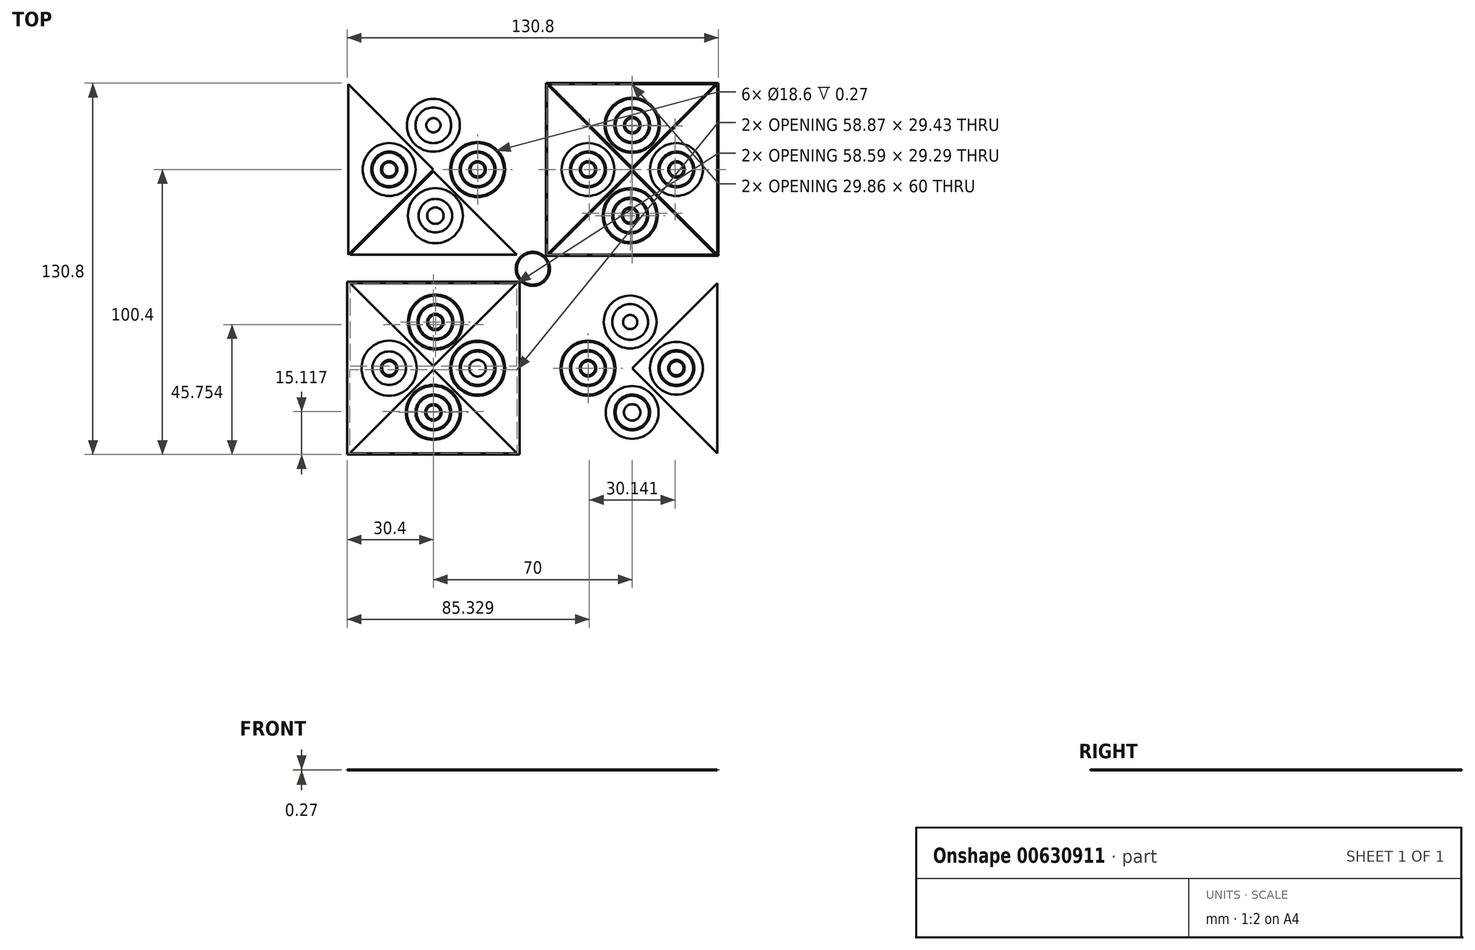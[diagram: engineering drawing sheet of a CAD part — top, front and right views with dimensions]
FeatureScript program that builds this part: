
annotation { "Feature Type Name" : "Feature", "Feature Type Description" : "" }
export const myFeature = defineFeature(function(context is Context, id is Id, definition is map)
    precondition{}
    {
        {
            var Q0;
            Q0=qCreatedBy(makeId("Top.planeOp"),FACE);
            var sketch = newSketch(context, id + "F0", { "sketchPlane" : qUnion([Q0])});
            skLineSegment(sketch, "E0.bottom", {"start": v(70, -70) * mm, "end": v(-70, -70) * mm});
            skLineSegment(sketch, "E0.top", {"start": v(70, 70) * mm, "end": v(-70, 70) * mm});
            skLineSegment(sketch, "E0.left", {"start": v(70, -70) * mm, "end": v(70, 70) * mm});
            skLineSegment(sketch, "E0.right", {"start": v(-70, -70) * mm, "end": v(-70, 70) * mm});
            skPoint(sketch, "E0.middle", {"position": v(0, 0) * mm});
            skLineSegment(sketch, "E1.bottom", {"start": v(-5.57, -65) * mm, "end": v(-64.43, -65) * mm});
            skLineSegment(sketch, "E1.top", {"start": v(-5.7, -5) * mm, "end": v(-64.3, -5) * mm});
            skLineSegment(sketch, "E1.left", {"start": v(-5, -65) * mm, "end": v(-5, -5) * mm});
            skLineSegment(sketch, "E1.right", {"start": v(-65, -65) * mm, "end": v(-65, -5) * mm});
            skPoint(sketch, "E1.middle", {"position": v(-35, -35) * mm});
            skLineSegment(sketch, "E2", {"start": v(-65, -5) * mm, "end": v(-35.14, -34.86) * mm});
            skLineSegment(sketch, "E3", {"start": v(-34.86, -35.14) * mm, "end": v(-5, -65) * mm});
            skLineSegment(sketch, "E4", {"start": v(-65, -65) * mm, "end": v(-35.14, -35.14) * mm});
            skLineSegment(sketch, "E5", {"start": v(-5, -5) * mm, "end": v(-34.86, -34.86) * mm});
            skLineSegment(sketch, "E6.0", {"start": v(-4.6, 0) * mm, "end": v(-70, 0) * mm});
            skLineSegment(sketch, "E6.1", {"start": v(0, -70) * mm, "end": v(0, -4.6) * mm});
            skLineSegment(sketch, "E6.2", {"start": v(0, -70) * mm, "end": v(-70, -70) * mm});
            skLineSegment(sketch, "E6.3", {"start": v(-70, -70) * mm, "end": v(-70, 0) * mm});
            skLineSegment(sketch, "E7.0", {"start": v(-4.6, -4.6) * mm, "end": v(-65.4, -4.6) * mm});
            skLineSegment(sketch, "E7.1", {"start": v(-4.6, -65.4) * mm, "end": v(-4.6, -4.6) * mm});
            skLineSegment(sketch, "E7.2", {"start": v(-4.6, -65.4) * mm, "end": v(-65.4, -65.4) * mm});
            skLineSegment(sketch, "E7.3", {"start": v(-65.4, -65.4) * mm, "end": v(-65.4, -4.6) * mm});
            skLineSegment(sketch, "E8.0", {"start": v(-35, -35.57) * mm, "end": v(-5.57, -65) * mm});
            skLineSegment(sketch, "E8.1", {"start": v(-64.43, -65) * mm, "end": v(-35, -35.57) * mm});
            skLineSegment(sketch, "E9.0", {"start": v(-64.3, -5) * mm, "end": v(-35, -34.3) * mm});
            skLineSegment(sketch, "E9.1", {"start": v(-5.7, -5) * mm, "end": v(-35, -34.3) * mm});
            skArc(sketch, "E10", {"start": v(-35.14, -34.86) * mm, "mid": v(-35.2, -35) * mm, "end": v(-35.14, -35.14) * mm});
            skArc(sketch, "E11.trimOffspring", {"start": v(-34.86, -35.14) * mm, "mid": v(-34.8, -35) * mm, "end": v(-34.86, -34.86) * mm});
            skPoint(sketch, "E12.MirrorCS.end.orphan", {"position": v(-11.42, -33.04) * mm});
            skPoint(sketch, "E12.MirrorCS.start.orphan", {"position": v(-26.98, -37.19) * mm});
            skPoint(sketch, "E13.end.orphan", {"position": v(-36.96, -58.58) * mm});
            skPoint(sketch, "E13.start.orphan", {"position": v(-32.81, -43.02) * mm});
            skCircle(sketch, "E14", {"center": v(-35, -50.57) * mm, "radius": 2.5 * mm});
            skCircle(sketch, "E15.0", {"center": v(-35, -50.57) * mm, "radius": 2.9 * mm});
            skCircle(sketch, "E16.0", {"center": v(-35, -50.57) * mm, "radius": 5.9 * mm});
            skCircle(sketch, "E17.0", {"center": v(-35, -50.57) * mm, "radius": 6.3 * mm});
            skCircle(sketch, "E18.0", {"center": v(-35, -50.57) * mm, "radius": 9.3 * mm});
            skCircle(sketch, "E19.0", {"center": v(-35, -50.57) * mm, "radius": 9.7 * mm});
            skCircle(sketch, "E20.MirrorC", {"center": v(-19.43, -35) * mm, "radius": 9.7 * mm});
            skCircle(sketch, "E21.MirrorC", {"center": v(-19.43, -35) * mm, "radius": 9.3 * mm});
            skCircle(sketch, "E22.MirrorC", {"center": v(-19.43, -35) * mm, "radius": 6.3 * mm});
            skCircle(sketch, "E23.MirrorC", {"center": v(-19.43, -35) * mm, "radius": 5.9 * mm});
            skCircle(sketch, "E24.MirrorC", {"center": v(-19.43, -35) * mm, "radius": 2.9 * mm});
            skCircle(sketch, "E25.MirrorC", {"center": v(-19.43, -35) * mm, "radius": 2.5 * mm});
            skCircle(sketch, "E26.MirrorC", {"center": v(-50.57, -35) * mm, "radius": 9.7 * mm});
            skCircle(sketch, "E27.MirrorC", {"center": v(-50.57, -35) * mm, "radius": 9.3 * mm});
            skCircle(sketch, "E28.MirrorC", {"center": v(-50.57, -35) * mm, "radius": 5.9 * mm});
            skCircle(sketch, "E29.MirrorC", {"center": v(-50.57, -35) * mm, "radius": 6.3 * mm});
            skCircle(sketch, "E30.MirrorC", {"center": v(-50.57, -35) * mm, "radius": 2.5 * mm});
            skCircle(sketch, "E31.MirrorC", {"center": v(-50.57, -35) * mm, "radius": 2.9 * mm});
            skCircle(sketch, "E32.MirrorC", {"center": v(-34.3, -18.73) * mm, "radius": 9.7 * mm});
            skCircle(sketch, "E33.MirrorC", {"center": v(-34.3, -18.73) * mm, "radius": 9.3 * mm});
            skCircle(sketch, "E34.MirrorC", {"center": v(-34.3, -18.73) * mm, "radius": 5.9 * mm});
            skCircle(sketch, "E35.MirrorC", {"center": v(-34.3, -18.73) * mm, "radius": 6.3 * mm});
            skCircle(sketch, "E36.MirrorC", {"center": v(-34.3, -18.73) * mm, "radius": 2.5 * mm});
            skCircle(sketch, "E37.MirrorC", {"center": v(-34.3, -18.73) * mm, "radius": 2.9 * mm});
            skArc(sketch, "E38.MirrorCS", {"start": v(-35.14, 34.86) * mm, "mid": v(-35.2, 35) * mm, "end": v(-35.14, 35.14) * mm});
            skArc(sketch, "E39.MirrorCS", {"start": v(-34.86, 35.14) * mm, "mid": v(-34.8, 35) * mm, "end": v(-34.86, 34.86) * mm});
            skCircle(sketch, "E40.MirrorC", {"center": v(-34.3, 18.73) * mm, "radius": 2.9 * mm});
            skCircle(sketch, "E41.MirrorC", {"center": v(-34.3, 18.73) * mm, "radius": 2.5 * mm});
            skCircle(sketch, "E42.MirrorC", {"center": v(-35, 50.57) * mm, "radius": 2.5 * mm});
            skCircle(sketch, "E43.MirrorC", {"center": v(-35, 50.57) * mm, "radius": 2.9 * mm});
            skCircle(sketch, "E44.MirrorC", {"center": v(-19.43, 35) * mm, "radius": 2.9 * mm});
            skCircle(sketch, "E45.MirrorC", {"center": v(-50.57, 35) * mm, "radius": 2.5 * mm});
            skCircle(sketch, "E46.MirrorC", {"center": v(-50.57, 35) * mm, "radius": 2.9 * mm});
            skCircle(sketch, "E47.MirrorC", {"center": v(-19.43, 35) * mm, "radius": 2.5 * mm});
            skCircle(sketch, "E48.MirrorC", {"center": v(-34.3, 18.73) * mm, "radius": 9.3 * mm});
            skLineSegment(sketch, "E49.MirrorCS", {"start": v(-5.57, 65) * mm, "end": v(-64.43, 65) * mm});
            skLineSegment(sketch, "E50.MirrorCS", {"start": v(-5.7, 5) * mm, "end": v(-64.3, 5) * mm});
            skLineSegment(sketch, "E51.MirrorCS", {"start": v(-5, 65) * mm, "end": v(-5, 5) * mm});
            skLineSegment(sketch, "E52.MirrorCS", {"start": v(-34.86, 35.14) * mm, "end": v(-5, 65) * mm});
            skLineSegment(sketch, "E53.MirrorCS", {"start": v(-65, 65) * mm, "end": v(-35.14, 35.14) * mm});
            skLineSegment(sketch, "E54.MirrorCS", {"start": v(-65.4, 65.4) * mm, "end": v(-65.4, 4.6) * mm});
            skCircle(sketch, "E55.MirrorC", {"center": v(-35, 50.57) * mm, "radius": 9.3 * mm});
            skPoint(sketch, "E56.MirrorP", {"position": v(-32.81, 43.02) * mm});
            skCircle(sketch, "E57.MirrorC", {"center": v(-50.57, 35) * mm, "radius": 5.9 * mm});
            skCircle(sketch, "E58.MirrorC", {"center": v(-35, 50.57) * mm, "radius": 6.3 * mm});
            skCircle(sketch, "E59.MirrorC", {"center": v(-19.43, 35) * mm, "radius": 5.9 * mm});
            skCircle(sketch, "E60.MirrorC", {"center": v(-34.3, 18.73) * mm, "radius": 9.7 * mm});
            skCircle(sketch, "E61.MirrorC", {"center": v(-35, 50.57) * mm, "radius": 5.9 * mm});
            skCircle(sketch, "E62.MirrorC", {"center": v(-34.3, 18.73) * mm, "radius": 5.9 * mm});
            skCircle(sketch, "E63.MirrorC", {"center": v(-50.57, 35) * mm, "radius": 6.3 * mm});
            skLineSegment(sketch, "E64.MirrorCS", {"start": v(-5.7, 5) * mm, "end": v(-35, 34.3) * mm});
            skCircle(sketch, "E65.MirrorC", {"center": v(-19.43, 35) * mm, "radius": 9.3 * mm});
            skCircle(sketch, "E66.MirrorC", {"center": v(-19.43, 35) * mm, "radius": 9.7 * mm});
            skLineSegment(sketch, "E67.MirrorCS", {"start": v(-4.6, 65.4) * mm, "end": v(-65.4, 65.4) * mm});
            skCircle(sketch, "E68.MirrorC", {"center": v(-50.57, 35) * mm, "radius": 9.7 * mm});
            skCircle(sketch, "E69.MirrorC", {"center": v(-35, 50.57) * mm, "radius": 9.7 * mm});
            skLineSegment(sketch, "E70.MirrorCS", {"start": v(-65, 65) * mm, "end": v(-65, 5) * mm});
            skLineSegment(sketch, "E71.MirrorCS", {"start": v(-65, 5) * mm, "end": v(-35.14, 34.86) * mm});
            skLineSegment(sketch, "E72.MirrorCS", {"start": v(-64.43, 65) * mm, "end": v(-35, 35.57) * mm});
            skPoint(sketch, "E73.MirrorP", {"position": v(-26.98, 37.19) * mm});
            skCircle(sketch, "E74.MirrorC", {"center": v(-19.43, 35) * mm, "radius": 6.3 * mm});
            skLineSegment(sketch, "E75.MirrorCS", {"start": v(-35, 35.57) * mm, "end": v(-5.57, 65) * mm});
            skLineSegment(sketch, "E76.MirrorCS", {"start": v(-5, 5) * mm, "end": v(-34.86, 34.86) * mm});
            skLineSegment(sketch, "E77.MirrorCS", {"start": v(-4.6, 4.6) * mm, "end": v(-65.4, 4.6) * mm});
            skCircle(sketch, "E78.MirrorC", {"center": v(-50.57, 35) * mm, "radius": 9.3 * mm});
            skPoint(sketch, "E79.MirrorP", {"position": v(-11.42, 33.04) * mm});
            skLineSegment(sketch, "E80.MirrorCS", {"start": v(-4.6, 65.4) * mm, "end": v(-4.6, 4.6) * mm});
            skPoint(sketch, "E81.MirrorP", {"position": v(-36.96, 58.58) * mm});
            skLineSegment(sketch, "E82.MirrorCS", {"start": v(-64.3, 5) * mm, "end": v(-35, 34.3) * mm});
            skCircle(sketch, "E83.MirrorC", {"center": v(-34.3, 18.73) * mm, "radius": 6.3 * mm});
            skArc(sketch, "E84.MirrorCS", {"start": v(35.14, -34.86) * mm, "mid": v(35.2, -35) * mm, "end": v(35.14, -35.14) * mm});
            skArc(sketch, "E85.MirrorCS", {"start": v(34.86, -35.14) * mm, "mid": v(34.8, -35) * mm, "end": v(34.86, -34.86) * mm});
            skArc(sketch, "E86.MirrorCS", {"start": v(35.14, 34.86) * mm, "mid": v(35.2, 35) * mm, "end": v(35.14, 35.14) * mm});
            skArc(sketch, "E87.MirrorCS", {"start": v(34.86, 35.14) * mm, "mid": v(34.8, 35) * mm, "end": v(34.86, 34.86) * mm});
            skCircle(sketch, "E88.MirrorC", {"center": v(34.3, -18.73) * mm, "radius": 2.5 * mm});
            skCircle(sketch, "E89.MirrorC", {"center": v(34.3, 18.73) * mm, "radius": 2.5 * mm});
            skCircle(sketch, "E90.MirrorC", {"center": v(34.3, -18.73) * mm, "radius": 2.9 * mm});
            skCircle(sketch, "E91.MirrorC", {"center": v(34.3, 18.73) * mm, "radius": 2.9 * mm});
            skCircle(sketch, "E92.MirrorC", {"center": v(35, -50.57) * mm, "radius": 2.9 * mm});
            skCircle(sketch, "E93.MirrorC", {"center": v(35, -50.57) * mm, "radius": 2.5 * mm});
            skCircle(sketch, "E94.MirrorC", {"center": v(50.57, -35) * mm, "radius": 2.5 * mm});
            skCircle(sketch, "E95.MirrorC", {"center": v(19.43, -35) * mm, "radius": 2.9 * mm});
            skCircle(sketch, "E96.MirrorC", {"center": v(19.43, 35) * mm, "radius": 2.5 * mm});
            skCircle(sketch, "E97.MirrorC", {"center": v(19.43, -35) * mm, "radius": 2.5 * mm});
            skCircle(sketch, "E98.MirrorC", {"center": v(50.57, -35) * mm, "radius": 2.9 * mm});
            skCircle(sketch, "E99.MirrorC", {"center": v(50.57, 35) * mm, "radius": 2.5 * mm});
            skCircle(sketch, "E100.MirrorC", {"center": v(35, 50.57) * mm, "radius": 2.5 * mm});
            skCircle(sketch, "E101.MirrorC", {"center": v(35, 50.57) * mm, "radius": 2.9 * mm});
            skCircle(sketch, "E102.MirrorC", {"center": v(19.43, 35) * mm, "radius": 2.9 * mm});
            skCircle(sketch, "E103.MirrorC", {"center": v(50.57, 35) * mm, "radius": 2.9 * mm});
            skLineSegment(sketch, "E104.MirrorCS", {"start": v(5, -5) * mm, "end": v(34.86, -34.86) * mm});
            skLineSegment(sketch, "E105.MirrorCS", {"start": v(5.57, 65) * mm, "end": v(64.43, 65) * mm});
            skCircle(sketch, "E106.MirrorC", {"center": v(35, -50.57) * mm, "radius": 6.3 * mm});
            skCircle(sketch, "E107.MirrorC", {"center": v(34.3, -18.73) * mm, "radius": 9.3 * mm});
            skLineSegment(sketch, "E108.MirrorCS", {"start": v(5.7, 5) * mm, "end": v(35, 34.3) * mm});
            skLineSegment(sketch, "E109.MirrorCS", {"start": v(65, 65) * mm, "end": v(65, 5) * mm});
            skLineSegment(sketch, "E110.MirrorCS", {"start": v(35, -35.57) * mm, "end": v(5.57, -65) * mm});
            skLineSegment(sketch, "E111.MirrorCS", {"start": v(35, 35.57) * mm, "end": v(5.57, 65) * mm});
            skCircle(sketch, "E112.MirrorC", {"center": v(34.3, 18.73) * mm, "radius": 9.7 * mm});
            skCircle(sketch, "E113.MirrorC", {"center": v(34.3, -18.73) * mm, "radius": 9.7 * mm});
            skCircle(sketch, "E114.MirrorC", {"center": v(35, -50.57) * mm, "radius": 5.9 * mm});
            skLineSegment(sketch, "E115.MirrorCS", {"start": v(4.6, 65.4) * mm, "end": v(4.6, 4.6) * mm});
            skLineSegment(sketch, "E116.MirrorCS", {"start": v(5.57, -65) * mm, "end": v(64.43, -65) * mm});
            skLineSegment(sketch, "E117.MirrorCS", {"start": v(64.3, -5) * mm, "end": v(35, -34.3) * mm});
            skLineSegment(sketch, "E118.MirrorCS", {"start": v(5, -65) * mm, "end": v(5, -5) * mm});
            skCircle(sketch, "E119.MirrorC", {"center": v(34.3, 18.73) * mm, "radius": 9.3 * mm});
            skLineSegment(sketch, "E120.MirrorCS", {"start": v(4.6, 4.6) * mm, "end": v(65.4, 4.6) * mm});
            skLineSegment(sketch, "E121.MirrorCS", {"start": v(65.4, -65.4) * mm, "end": v(65.4, -4.6) * mm});
            skLineSegment(sketch, "E122.MirrorCS", {"start": v(5.7, -5) * mm, "end": v(64.3, -5) * mm});
            skCircle(sketch, "E123.MirrorC", {"center": v(35, 50.57) * mm, "radius": 5.9 * mm});
            skLineSegment(sketch, "E124.MirrorCS", {"start": v(5.7, 5) * mm, "end": v(64.3, 5) * mm});
            skCircle(sketch, "E125.MirrorC", {"center": v(19.43, -35) * mm, "radius": 9.7 * mm});
            skLineSegment(sketch, "E126.MirrorCS", {"start": v(64.43, -65) * mm, "end": v(35, -35.57) * mm});
            skLineSegment(sketch, "E127.MirrorCS", {"start": v(5.7, -5) * mm, "end": v(35, -34.3) * mm});
            skCircle(sketch, "E128.MirrorC", {"center": v(35, 50.57) * mm, "radius": 6.3 * mm});
            skLineSegment(sketch, "E129.MirrorCS", {"start": v(4.6, -65.4) * mm, "end": v(65.4, -65.4) * mm});
            skLineSegment(sketch, "E130.MirrorCS", {"start": v(65.4, 65.4) * mm, "end": v(65.4, 4.6) * mm});
            skLineSegment(sketch, "E131.MirrorCS", {"start": v(65, -5) * mm, "end": v(35.14, -34.86) * mm});
            skLineSegment(sketch, "E132.MirrorCS", {"start": v(34.86, -35.14) * mm, "end": v(5, -65) * mm});
            skCircle(sketch, "E133.MirrorC", {"center": v(50.57, -35) * mm, "radius": 5.9 * mm});
            skCircle(sketch, "E134.MirrorC", {"center": v(34.3, 18.73) * mm, "radius": 5.9 * mm});
            skCircle(sketch, "E135.MirrorC", {"center": v(19.43, 35) * mm, "radius": 9.3 * mm});
            skCircle(sketch, "E136.MirrorC", {"center": v(50.57, 35) * mm, "radius": 9.3 * mm});
            skLineSegment(sketch, "E137.MirrorCS", {"start": v(4.6, -4.6) * mm, "end": v(65.4, -4.6) * mm});
            skCircle(sketch, "E138.MirrorC", {"center": v(19.43, 35) * mm, "radius": 5.9 * mm});
            skLineSegment(sketch, "E139.MirrorCS", {"start": v(4.6, -65.4) * mm, "end": v(4.6, -4.6) * mm});
            skCircle(sketch, "E140.MirrorC", {"center": v(35, 50.57) * mm, "radius": 9.7 * mm});
            skCircle(sketch, "E141.MirrorC", {"center": v(50.57, 35) * mm, "radius": 9.7 * mm});
            skLineSegment(sketch, "E142.MirrorCS", {"start": v(65, -65) * mm, "end": v(35.14, -35.14) * mm});
            skLineSegment(sketch, "E143.MirrorCS", {"start": v(5, 65) * mm, "end": v(5, 5) * mm});
            skCircle(sketch, "E144.MirrorC", {"center": v(34.3, -18.73) * mm, "radius": 6.3 * mm});
            skPoint(sketch, "E145.MirrorP", {"position": v(11.42, 33.04) * mm});
            skPoint(sketch, "E146.MirrorP", {"position": v(36.96, 58.58) * mm});
            skCircle(sketch, "E147.MirrorC", {"center": v(35, -50.57) * mm, "radius": 9.3 * mm});
            skCircle(sketch, "E148.MirrorC", {"center": v(19.43, 35) * mm, "radius": 9.7 * mm});
            skCircle(sketch, "E149.MirrorC", {"center": v(35, -50.57) * mm, "radius": 9.7 * mm});
            skCircle(sketch, "E150.MirrorC", {"center": v(50.57, -35) * mm, "radius": 6.3 * mm});
            skCircle(sketch, "E151.MirrorC", {"center": v(19.43, 35) * mm, "radius": 6.3 * mm});
            skCircle(sketch, "E152.MirrorC", {"center": v(34.3, 18.73) * mm, "radius": 6.3 * mm});
            skCircle(sketch, "E153.MirrorC", {"center": v(19.43, -35) * mm, "radius": 9.3 * mm});
            skPoint(sketch, "E154.MirrorP", {"position": v(11.42, -33.04) * mm});
            skCircle(sketch, "E155.MirrorC", {"center": v(19.43, -35) * mm, "radius": 6.3 * mm});
            skLineSegment(sketch, "E156.MirrorCS", {"start": v(65, 65) * mm, "end": v(35.14, 35.14) * mm});
            skLineSegment(sketch, "E157.MirrorCS", {"start": v(34.86, 35.14) * mm, "end": v(5, 65) * mm});
            skCircle(sketch, "E158.MirrorC", {"center": v(19.43, -35) * mm, "radius": 5.9 * mm});
            skLineSegment(sketch, "E159.MirrorCS", {"start": v(4.6, 65.4) * mm, "end": v(65.4, 65.4) * mm});
            skLineSegment(sketch, "E160.MirrorCS", {"start": v(64.43, 65) * mm, "end": v(35, 35.57) * mm});
            skPoint(sketch, "E161.MirrorP", {"position": v(32.81, -43.02) * mm});
            skCircle(sketch, "E162.MirrorC", {"center": v(35, 50.57) * mm, "radius": 9.3 * mm});
            skCircle(sketch, "E163.MirrorC", {"center": v(50.57, -35) * mm, "radius": 9.7 * mm});
            skCircle(sketch, "E164.MirrorC", {"center": v(34.3, -18.73) * mm, "radius": 5.9 * mm});
            skLineSegment(sketch, "E165.MirrorCS", {"start": v(65, 5) * mm, "end": v(35.14, 34.86) * mm});
            skLineSegment(sketch, "E166.MirrorCS", {"start": v(64.3, 5) * mm, "end": v(35, 34.3) * mm});
            skLineSegment(sketch, "E167.MirrorCS", {"start": v(65, -65) * mm, "end": v(65, -5) * mm});
            skPoint(sketch, "E168.MirrorP", {"position": v(26.98, -37.19) * mm});
            skCircle(sketch, "E169.MirrorC", {"center": v(50.57, -35) * mm, "radius": 9.3 * mm});
            skLineSegment(sketch, "E170.MirrorCS", {"start": v(5, 5) * mm, "end": v(34.86, 34.86) * mm});
            skCircle(sketch, "E171.MirrorC", {"center": v(50.57, 35) * mm, "radius": 5.9 * mm});
            skPoint(sketch, "E172.MirrorP", {"position": v(26.98, 37.19) * mm});
            skCircle(sketch, "E173.MirrorC", {"center": v(50.57, 35) * mm, "radius": 6.3 * mm});
            skPoint(sketch, "E174.MirrorP", {"position": v(36.96, -58.58) * mm});
            skPoint(sketch, "E175.MirrorP", {"position": v(32.81, 43.02) * mm});
            skCircle(sketch, "E176", {"center": v(0, 0) * mm, "radius": 5 * mm});
            skCircle(sketch, "E177.0", {"center": v(0, 0) * mm, "radius": 4.6 * mm});
            skSolve(sketch);
        }
        {
            var Q0;
            Q0=makeQuery(id+"F0.imprint","IMPRINT",FACE,{"disambiguationData":[TD([[makeQuery(id+"F0.imprint","IMPRINT",EDGE,{"derivedFrom":sQuery(id+"F0.wireOp",EDGE,"E84.MirrorCS")}),-1.0]])]});
            var Q1;
            Q1=makeQuery(id+"F0.imprint","IMPRINT",FACE,{"disambiguationData":[TD([[makeQuery(id+"F0.imprint","IMPRINT",EDGE,{"derivedFrom":sQuery(id+"F0.wireOp",EDGE,"E88.MirrorC")}),1.0]])]});
            var Q2;
            Q2=makeQuery(id+"F0.imprint","IMPRINT",FACE,{"disambiguationData":[TD([[makeQuery(id+"F0.imprint","IMPRINT",EDGE,{"derivedFrom":sQuery(id+"F0.wireOp",EDGE,"E144.MirrorC")}),-1.0]])]});
            var Q3;
            Q3=makeQuery(id+"F0.imprint","IMPRINT",FACE,{"disambiguationData":[TD([[makeQuery(id+"F0.imprint","IMPRINT",EDGE,{"derivedFrom":sQuery(id+"F0.wireOp",EDGE,"E107.MirrorC")}),1.0]])]});
            var Q4;
            Q4=makeQuery(id+"F0.imprint","IMPRINT",FACE,{"disambiguationData":[TD([[makeQuery(id+"F0.imprint","IMPRINT",EDGE,{"derivedFrom":sQuery(id+"F0.wireOp",EDGE,"E163.MirrorC")}),1.0]])]});
            var Q5;
            Q5=makeQuery(id+"F0.imprint","IMPRINT",FACE,{"disambiguationData":[TD([[makeQuery(id+"F0.imprint","IMPRINT",EDGE,{"derivedFrom":sQuery(id+"F0.wireOp",EDGE,"E133.MirrorC")}),-1.0]])]});
            var Q6;
            Q6=makeQuery(id+"F0.imprint","IMPRINT",FACE,{"disambiguationData":[TD([[makeQuery(id+"F0.imprint","IMPRINT",EDGE,{"derivedFrom":sQuery(id+"F0.wireOp",EDGE,"E94.MirrorC")}),-1.0]])]});
            var Q7;
            Q7=makeQuery(id+"F0.imprint","IMPRINT",FACE,{"disambiguationData":[TD([[makeQuery(id+"F0.imprint","IMPRINT",EDGE,{"derivedFrom":sQuery(id+"F0.wireOp",EDGE,"E125.MirrorC")}),1.0]])]});
            var Q8;
            Q8=makeQuery(id+"F0.imprint","IMPRINT",FACE,{"disambiguationData":[TD([[makeQuery(id+"F0.imprint","IMPRINT",EDGE,{"derivedFrom":sQuery(id+"F0.wireOp",EDGE,"E155.MirrorC")}),1.0]])]});
            var Q9;
            Q9=makeQuery(id+"F0.imprint","IMPRINT",FACE,{"disambiguationData":[TD([[makeQuery(id+"F0.imprint","IMPRINT",EDGE,{"derivedFrom":sQuery(id+"F0.wireOp",EDGE,"E95.MirrorC")}),1.0]])]});
            var Q10;
            Q10=makeQuery(id+"F0.imprint","IMPRINT",FACE,{"disambiguationData":[TD([[makeQuery(id+"F0.imprint","IMPRINT",EDGE,{"derivedFrom":sQuery(id+"F0.wireOp",EDGE,"E147.MirrorC")}),1.0]])]});
            var Q11;
            Q11=makeQuery(id+"F0.imprint","IMPRINT",FACE,{"disambiguationData":[TD([[makeQuery(id+"F0.imprint","IMPRINT",EDGE,{"derivedFrom":sQuery(id+"F0.wireOp",EDGE,"E106.MirrorC")}),-1.0]])]});
            var Q12;
            Q12=makeQuery(id+"F0.imprint","IMPRINT",FACE,{"disambiguationData":[TD([[makeQuery(id+"F0.imprint","IMPRINT",EDGE,{"derivedFrom":sQuery(id+"F0.wireOp",EDGE,"E92.MirrorC")}),-1.0]])]});
            var Q13;
            Q13=makeQuery(id+"F0.imprint","IMPRINT",FACE,{"disambiguationData":[TD([[makeQuery(id+"F0.imprint","IMPRINT",EDGE,{"derivedFrom":sQuery(id+"F0.wireOp",EDGE,"E1.bottom")}),1.0]])]});
            var Q14;
            Q14=makeQuery(id+"F0.imprint","IMPRINT",FACE,{"disambiguationData":[TD([[makeQuery(id+"F0.imprint","IMPRINT",EDGE,{"derivedFrom":sQuery(id+"F0.wireOp",EDGE,"E32.MirrorC")}),1.0]])]});
            var Q15;
            Q15=makeQuery(id+"F0.imprint","IMPRINT",FACE,{"disambiguationData":[TD([[makeQuery(id+"F0.imprint","IMPRINT",EDGE,{"derivedFrom":sQuery(id+"F0.wireOp",EDGE,"E34.MirrorC")}),-1.0]])]});
            var Q16;
            Q16=makeQuery(id+"F0.imprint","IMPRINT",FACE,{"disambiguationData":[TD([[makeQuery(id+"F0.imprint","IMPRINT",EDGE,{"derivedFrom":sQuery(id+"F0.wireOp",EDGE,"E36.MirrorC")}),-1.0]])]});
            var Q17;
            Q17=makeQuery(id+"F0.imprint","IMPRINT",FACE,{"disambiguationData":[TD([[makeQuery(id+"F0.imprint","IMPRINT",EDGE,{"derivedFrom":sQuery(id+"F0.wireOp",EDGE,"E20.MirrorC")}),-1.0]])]});
            var Q18;
            Q18=makeQuery(id+"F0.imprint","IMPRINT",FACE,{"disambiguationData":[TD([[makeQuery(id+"F0.imprint","IMPRINT",EDGE,{"derivedFrom":sQuery(id+"F0.wireOp",EDGE,"E22.MirrorC")}),-1.0]])]});
            var Q19;
            Q19=makeQuery(id+"F0.imprint","IMPRINT",FACE,{"disambiguationData":[TD([[makeQuery(id+"F0.imprint","IMPRINT",EDGE,{"derivedFrom":sQuery(id+"F0.wireOp",EDGE,"E24.MirrorC")}),-1.0]])]});
            var Q20;
            Q20=makeQuery(id+"F0.imprint","IMPRINT",FACE,{"disambiguationData":[TD([[makeQuery(id+"F0.imprint","IMPRINT",EDGE,{"derivedFrom":sQuery(id+"F0.wireOp",EDGE,"E18.0")}),-1.0]])]});
            var Q21;
            Q21=makeQuery(id+"F0.imprint","IMPRINT",FACE,{"disambiguationData":[TD([[makeQuery(id+"F0.imprint","IMPRINT",EDGE,{"derivedFrom":sQuery(id+"F0.wireOp",EDGE,"E16.0")}),-1.0]])]});
            var Q22;
            Q22=makeQuery(id+"F0.imprint","IMPRINT",FACE,{"disambiguationData":[TD([[makeQuery(id+"F0.imprint","IMPRINT",EDGE,{"derivedFrom":sQuery(id+"F0.wireOp",EDGE,"E14")}),-1.0]])]});
            var Q23;
            Q23=makeQuery(id+"F0.imprint","IMPRINT",FACE,{"disambiguationData":[TD([[makeQuery(id+"F0.imprint","IMPRINT",EDGE,{"derivedFrom":sQuery(id+"F0.wireOp",EDGE,"E26.MirrorC")}),-1.0]])]});
            var Q24;
            Q24=makeQuery(id+"F0.imprint","IMPRINT",FACE,{"disambiguationData":[TD([[makeQuery(id+"F0.imprint","IMPRINT",EDGE,{"derivedFrom":sQuery(id+"F0.wireOp",EDGE,"E28.MirrorC")}),1.0]])]});
            var Q25;
            Q25=makeQuery(id+"F0.imprint","IMPRINT",FACE,{"disambiguationData":[TD([[makeQuery(id+"F0.imprint","IMPRINT",EDGE,{"derivedFrom":sQuery(id+"F0.wireOp",EDGE,"E30.MirrorC")}),1.0]])]});
            var Q26;
            Q26=makeQuery(id+"F0.imprint","IMPRINT",FACE,{"disambiguationData":[TD([[makeQuery(id+"F0.imprint","IMPRINT",EDGE,{"derivedFrom":sQuery(id+"F0.wireOp",EDGE,"E38.MirrorCS")}),-1.0]])]});
            var Q27;
            Q27=makeQuery(id+"F0.imprint","IMPRINT",FACE,{"disambiguationData":[TD([[makeQuery(id+"F0.imprint","IMPRINT",EDGE,{"derivedFrom":sQuery(id+"F0.wireOp",EDGE,"E68.MirrorC")}),1.0]])]});
            var Q28;
            Q28=makeQuery(id+"F0.imprint","IMPRINT",FACE,{"disambiguationData":[TD([[makeQuery(id+"F0.imprint","IMPRINT",EDGE,{"derivedFrom":sQuery(id+"F0.wireOp",EDGE,"E57.MirrorC")}),-1.0]])]});
            var Q29;
            Q29=makeQuery(id+"F0.imprint","IMPRINT",FACE,{"disambiguationData":[TD([[makeQuery(id+"F0.imprint","IMPRINT",EDGE,{"derivedFrom":sQuery(id+"F0.wireOp",EDGE,"E45.MirrorC")}),-1.0]])]});
            var Q30;
            Q30=makeQuery(id+"F0.imprint","IMPRINT",FACE,{"disambiguationData":[TD([[makeQuery(id+"F0.imprint","IMPRINT",EDGE,{"derivedFrom":sQuery(id+"F0.wireOp",EDGE,"E60.MirrorC")}),-1.0]])]});
            var Q31;
            Q31=makeQuery(id+"F0.imprint","IMPRINT",FACE,{"disambiguationData":[TD([[makeQuery(id+"F0.imprint","IMPRINT",EDGE,{"derivedFrom":sQuery(id+"F0.wireOp",EDGE,"E62.MirrorC")}),1.0]])]});
            var Q32;
            Q32=makeQuery(id+"F0.imprint","IMPRINT",FACE,{"disambiguationData":[TD([[makeQuery(id+"F0.imprint","IMPRINT",EDGE,{"derivedFrom":sQuery(id+"F0.wireOp",EDGE,"E40.MirrorC")}),-1.0]])]});
            var Q33;
            Q33=makeQuery(id+"F0.imprint","IMPRINT",FACE,{"disambiguationData":[TD([[makeQuery(id+"F0.imprint","IMPRINT",EDGE,{"derivedFrom":sQuery(id+"F0.wireOp",EDGE,"E65.MirrorC")}),-1.0]])]});
            var Q34;
            Q34=makeQuery(id+"F0.imprint","IMPRINT",FACE,{"disambiguationData":[TD([[makeQuery(id+"F0.imprint","IMPRINT",EDGE,{"derivedFrom":sQuery(id+"F0.wireOp",EDGE,"E59.MirrorC")}),-1.0]])]});
            var Q35;
            Q35=makeQuery(id+"F0.imprint","IMPRINT",FACE,{"disambiguationData":[TD([[makeQuery(id+"F0.imprint","IMPRINT",EDGE,{"derivedFrom":sQuery(id+"F0.wireOp",EDGE,"E44.MirrorC")}),1.0]])]});
            var Q36;
            Q36=makeQuery(id+"F0.imprint","IMPRINT",FACE,{"disambiguationData":[TD([[makeQuery(id+"F0.imprint","IMPRINT",EDGE,{"derivedFrom":sQuery(id+"F0.wireOp",EDGE,"E55.MirrorC")}),1.0]])]});
            var Q37;
            Q37=makeQuery(id+"F0.imprint","IMPRINT",FACE,{"disambiguationData":[TD([[makeQuery(id+"F0.imprint","IMPRINT",EDGE,{"derivedFrom":sQuery(id+"F0.wireOp",EDGE,"E58.MirrorC")}),-1.0]])]});
            var Q38;
            Q38=makeQuery(id+"F0.imprint","IMPRINT",FACE,{"disambiguationData":[TD([[makeQuery(id+"F0.imprint","IMPRINT",EDGE,{"derivedFrom":sQuery(id+"F0.wireOp",EDGE,"E42.MirrorC")}),1.0]])]});
            var Q39;
            Q39=makeQuery(id+"F0.imprint","IMPRINT",FACE,{"disambiguationData":[TD([[makeQuery(id+"F0.imprint","IMPRINT",EDGE,{"derivedFrom":sQuery(id+"F0.wireOp",EDGE,"E86.MirrorCS")}),1.0]])]});
            var Q40;
            Q40=makeQuery(id+"F0.imprint","IMPRINT",FACE,{"disambiguationData":[TD([[makeQuery(id+"F0.imprint","IMPRINT",EDGE,{"derivedFrom":sQuery(id+"F0.wireOp",EDGE,"E119.MirrorC")}),-1.0]])]});
            var Q41;
            Q41=makeQuery(id+"F0.imprint","IMPRINT",FACE,{"disambiguationData":[TD([[makeQuery(id+"F0.imprint","IMPRINT",EDGE,{"derivedFrom":sQuery(id+"F0.wireOp",EDGE,"E134.MirrorC")}),-1.0]])]});
            var Q42;
            Q42=makeQuery(id+"F0.imprint","IMPRINT",FACE,{"disambiguationData":[TD([[makeQuery(id+"F0.imprint","IMPRINT",EDGE,{"derivedFrom":sQuery(id+"F0.wireOp",EDGE,"E89.MirrorC")}),-1.0]])]});
            var Q43;
            Q43=makeQuery(id+"F0.imprint","IMPRINT",FACE,{"disambiguationData":[TD([[makeQuery(id+"F0.imprint","IMPRINT",EDGE,{"derivedFrom":sQuery(id+"F0.wireOp",EDGE,"E135.MirrorC")}),1.0]])]});
            var Q44;
            Q44=makeQuery(id+"F0.imprint","IMPRINT",FACE,{"disambiguationData":[TD([[makeQuery(id+"F0.imprint","IMPRINT",EDGE,{"derivedFrom":sQuery(id+"F0.wireOp",EDGE,"E138.MirrorC")}),1.0]])]});
            var Q45;
            Q45=makeQuery(id+"F0.imprint","IMPRINT",FACE,{"disambiguationData":[TD([[makeQuery(id+"F0.imprint","IMPRINT",EDGE,{"derivedFrom":sQuery(id+"F0.wireOp",EDGE,"E96.MirrorC")}),1.0]])]});
            var Q46;
            Q46=makeQuery(id+"F0.imprint","IMPRINT",FACE,{"disambiguationData":[TD([[makeQuery(id+"F0.imprint","IMPRINT",EDGE,{"derivedFrom":sQuery(id+"F0.wireOp",EDGE,"E100.MirrorC")}),-1.0]])]});
            var Q47;
            Q47=makeQuery(id+"F0.imprint","IMPRINT",FACE,{"disambiguationData":[TD([[makeQuery(id+"F0.imprint","IMPRINT",EDGE,{"derivedFrom":sQuery(id+"F0.wireOp",EDGE,"E123.MirrorC")}),-1.0]])]});
            var Q48;
            Q48=makeQuery(id+"F0.imprint","IMPRINT",FACE,{"disambiguationData":[TD([[makeQuery(id+"F0.imprint","IMPRINT",EDGE,{"derivedFrom":sQuery(id+"F0.wireOp",EDGE,"E140.MirrorC")}),1.0]])]});
            var Q49;
            Q49=makeQuery(id+"F0.imprint","IMPRINT",FACE,{"disambiguationData":[TD([[makeQuery(id+"F0.imprint","IMPRINT",EDGE,{"derivedFrom":sQuery(id+"F0.wireOp",EDGE,"E136.MirrorC")}),1.0]])]});
            var Q50;
            Q50=makeQuery(id+"F0.imprint","IMPRINT",FACE,{"disambiguationData":[TD([[makeQuery(id+"F0.imprint","IMPRINT",EDGE,{"derivedFrom":sQuery(id+"F0.wireOp",EDGE,"E171.MirrorC")}),1.0]])]});
            var Q51;
            Q51=makeQuery(id+"F0.imprint","IMPRINT",FACE,{"disambiguationData":[TD([[makeQuery(id+"F0.imprint","IMPRINT",EDGE,{"derivedFrom":sQuery(id+"F0.wireOp",EDGE,"E99.MirrorC")}),1.0]])]});
            extrude(context, id + "F1", {"entities" : qUnion([Q0, Q1, Q2, Q3, Q4, Q5, Q6, Q7, Q8, Q9, Q10, Q11, Q12, Q13, Q14, Q15, Q16, Q17, Q18, Q19, Q20, Q21, Q22, Q23, Q24, Q25, Q26, Q27, Q28, Q29, Q30, Q31, Q32, Q33, Q34, Q35, Q36, Q37, Q38, Q39, Q40, Q41, Q42, Q43, Q44, Q45, Q46, Q47, Q48, Q49, Q50, Q51]), "depth" : 0.27 * mm, "offsetDistance" : 25 * mm});
        }
        {
            var Q0;
            Q0=qCreatedBy(makeId("Top.planeOp"),FACE);
            var sketch = newSketch(context, id + "F2", { "sketchPlane" : qUnion([Q0])});
            skCircle(sketch, "E178", {"center": v(0, 0) * mm, "radius": 6 * mm});
            skCircle(sketch, "E179.0", {"center": v(0, 0) * mm, "radius": 5.6 * mm});
            skSolve(sketch);
        }
        {
            var Q0;
            Q0 = qSketchRegion(id + "F2", true);
            extrude(context, id + "F3", {"entities" : qUnion([Q0]), "depth" : 0.27 * mm, "offsetDistance" : 25 * mm});
        }
    });
